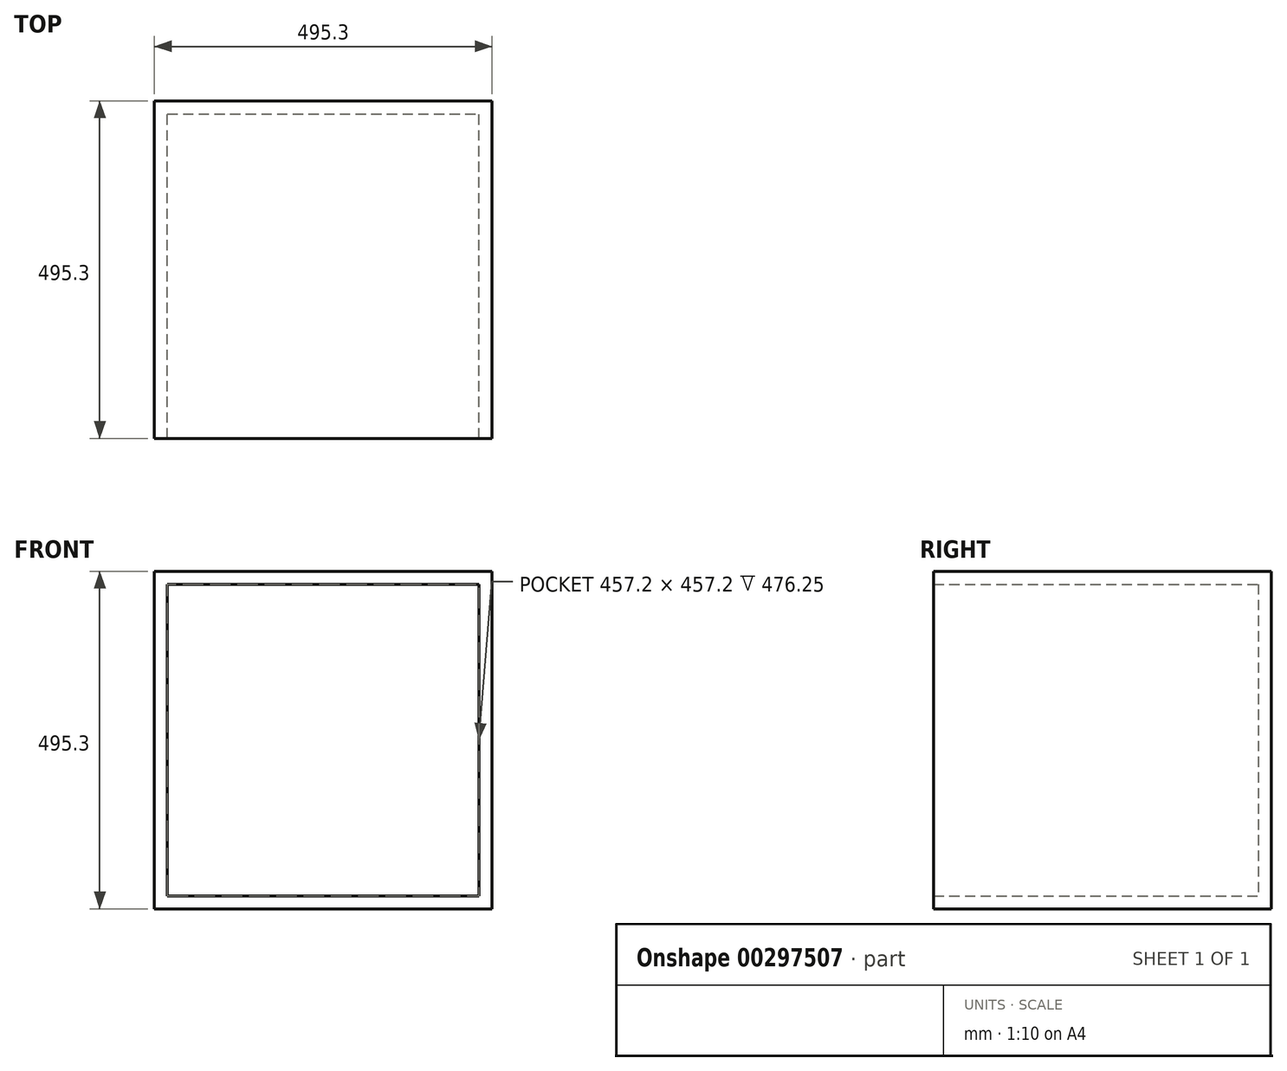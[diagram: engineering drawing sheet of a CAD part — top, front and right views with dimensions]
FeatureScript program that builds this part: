
annotation { "Feature Type Name" : "Feature", "Feature Type Description" : "" }
export const myFeature = defineFeature(function(context is Context, id is Id, definition is map)
    precondition{}
    {
        {
            var Q0;
            Q0=qCreatedBy(makeId("Top.planeOp"),FACE);
            var sketch = newSketch(context, id + "F0", { "sketchPlane" : qUnion([Q0])});
            skLineSegment(sketch, "E0.bottom", {"start": v(0, 0) * mm, "end": v(406.4, 0) * mm});
            skLineSegment(sketch, "E0.top", {"start": v(0, 406.4) * mm, "end": v(406.4, 406.4) * mm});
            skLineSegment(sketch, "E0.left", {"start": v(0, 0) * mm, "end": v(0, 406.4) * mm});
            skLineSegment(sketch, "E0.right", {"start": v(406.4, 0) * mm, "end": v(406.4, 406.4) * mm});
            skLineSegment(sketch, "E1.0", {"start": v(-25.4, 431.8) * mm, "end": v(431.8, 431.8) * mm});
            skLineSegment(sketch, "E1.1", {"start": v(-25.4, -25.4) * mm, "end": v(-25.4, 431.8) * mm});
            skLineSegment(sketch, "E1.2", {"start": v(-25.4, -25.4) * mm, "end": v(431.8, -25.4) * mm});
            skLineSegment(sketch, "E1.3", {"start": v(431.8, -25.4) * mm, "end": v(431.8, 431.8) * mm});
            skLineSegment(sketch, "E2.0", {"start": v(-44.45, 450.85) * mm, "end": v(450.85, 450.85) * mm});
            skLineSegment(sketch, "E2.1", {"start": v(-44.45, -44.45) * mm, "end": v(-44.45, 450.85) * mm});
            skLineSegment(sketch, "E2.2", {"start": v(-44.45, -44.45) * mm, "end": v(450.85, -44.45) * mm});
            skLineSegment(sketch, "E2.3", {"start": v(450.85, -44.45) * mm, "end": v(450.85, 450.85) * mm});
            skSolve(sketch);
        }
        {
            var Q0;
            Q0 = qSketchRegion(id + "F0", true);
            var Q1;
            Q1=makeQuery(id+"F0.imprint","IMPRINT",FACE,{"disambiguationData":[TD([[makeQuery(id+"F0.imprint","IMPRINT",EDGE,{"derivedFrom":sQuery(id+"F0.wireOp",EDGE,"E0.bottom")}),-1.0]])]});
            var Q2;
            Q2=makeQuery(id+"F0.imprint","IMPRINT",FACE,{"disambiguationData":[TD([[makeQuery(id+"F0.imprint","IMPRINT",EDGE,{"derivedFrom":sQuery(id+"F0.wireOp",EDGE,"E0.bottom")}),1.0]])]});
            extrude(context, id + "F1", {"entities" : qUnion([Q0, Q1, Q2]), "depth" : 19.05 * mm});
        }
        {
            var Q0;
            Q0=makeQuery(id+"F1.opExtrude","CAP_FACE",FACE,{"disambiguationData":[OSD([sQuery(id+"F0.wireOp",EDGE,"E2.0"),sQuery(id+"F0.wireOp",EDGE,"E2.1"),sQuery(id+"F0.wireOp",EDGE,"E2.2"),sQuery(id+"F0.wireOp",EDGE,"E2.3")])],"isStart":false});
            var sketch = newSketch(context, id + "F2", { "sketchPlane" : qUnion([Q0])});
            skLineSegment(sketch, "E3.0", {"start": v(-25.4, 431.8) * mm, "end": v(431.8, 431.8) * mm});
            skLineSegment(sketch, "E3.1", {"start": v(-25.4, -25.4) * mm, "end": v(-25.4, 431.8) * mm});
            skLineSegment(sketch, "E3.2", {"start": v(-25.4, -25.4) * mm, "end": v(431.8, -25.4) * mm});
            skLineSegment(sketch, "E3.3", {"start": v(431.8, -25.4) * mm, "end": v(431.8, 431.8) * mm});
            skSolve(sketch);
        }
        {
            var Q0;
            Q0=makeQuery(id+"F2.imprint","IMPRINT",FACE,{"disambiguationData":[TD([[makeQuery(id+"F2.imprint","IMPRINT",EDGE,{"derivedFrom":sQuery(id+"F2.wireOp",EDGE,"E3.0")}),1.0]])]});
            extrude(context, id + "F3", {"entities" : qUnion([Q0]), "operationType" : NewBodyOperationType.ADD, "depth" : 476.25 * mm});
        }
        {
            var Q0;
            Q0=makeQuery(id+"F3.opExtrude","CAP_FACE",FACE,{"disambiguationData":[OSD([sQuery(id+"F0.wireOp",EDGE,"E2.0"),sQuery(id+"F0.wireOp",EDGE,"E2.1"),sQuery(id+"F0.wireOp",EDGE,"E2.2"),sQuery(id+"F0.wireOp",EDGE,"E2.3"),sQuery(id+"F2.wireOp",EDGE,"E3.0"),sQuery(id+"F2.wireOp",EDGE,"E3.1"),sQuery(id+"F2.wireOp",EDGE,"E3.2"),sQuery(id+"F2.wireOp",EDGE,"E3.3")])],"isStart":false});
            var sketch = newSketch(context, id + "F4", { "sketchPlane" : qUnion([Q0])});
            skLineSegment(sketch, "E4.bottom", {"start": v(-25.4, 431.8) * mm, "end": v(431.8, 431.8) * mm});
            skLineSegment(sketch, "E4.top", {"start": v(-25.4, -25.4) * mm, "end": v(431.8, -25.4) * mm});
            skLineSegment(sketch, "E4.left", {"start": v(-25.4, 431.8) * mm, "end": v(-25.4, -25.4) * mm});
            skLineSegment(sketch, "E4.right", {"start": v(431.8, 431.8) * mm, "end": v(431.8, -25.4) * mm});
            skSolve(sketch);
        }
        {
            var Q0;
            Q0=makeQuery(id+"F4.imprint","IMPRINT",FACE,{"disambiguationData":[TD([[makeQuery(id+"F4.imprint","IMPRINT",EDGE,{"derivedFrom":sQuery(id+"F4.wireOp",EDGE,"E4.bottom")}),-1.0]])]});
            extrude(context, id + "F5", {"entities" : qUnion([Q0]), "operationType" : NewBodyOperationType.ADD, "oppositeDirection" : true, "depth" : 19.05 * mm});
        }
        {
            var Q0;
            {var subQ0=sQuery(id+"F0.wireOp",EDGE,"E2.2");Q0=makeQuery(id+"F3.boolean.opBoolean","MERGE",FACE,{"derivedFrom":[makeQuery(id+"F1.opExtrude","SWEPT_FACE",FACE,{"disambiguationData":[OSD([subQ0])]}),makeQuery(id+"F3.opExtrude","SWEPT_FACE",FACE,{"disambiguationData":[OSD([subQ0])]})]});}
            var sketch = newSketch(context, id + "F6", { "sketchPlane" : qUnion([Q0])});
            skLineSegment(sketch, "E5.0", {"start": v(-25.4, 476.25) * mm, "end": v(431.8, 476.25) * mm});
            skLineSegment(sketch, "E5.1", {"start": v(-25.4, 476.25) * mm, "end": v(-25.4, 19.05) * mm});
            skLineSegment(sketch, "E5.2", {"start": v(-25.4, 19.05) * mm, "end": v(431.8, 19.05) * mm});
            skLineSegment(sketch, "E5.3", {"start": v(431.8, 476.25) * mm, "end": v(431.8, 19.05) * mm});
            skSolve(sketch);
        }
        {
            var Q0;
            Q0=makeQuery(id+"F6.imprint","IMPRINT",FACE,{"disambiguationData":[TD([[makeQuery(id+"F6.imprint","IMPRINT",EDGE,{"derivedFrom":sQuery(id+"F6.wireOp",EDGE,"E5.0")}),-1.0]])]});
            extrude(context, id + "F7", {"entities" : qUnion([Q0]), "operationType" : NewBodyOperationType.REMOVE, "oppositeDirection" : true, "depth" : 25.4 * mm});
        }
    });
